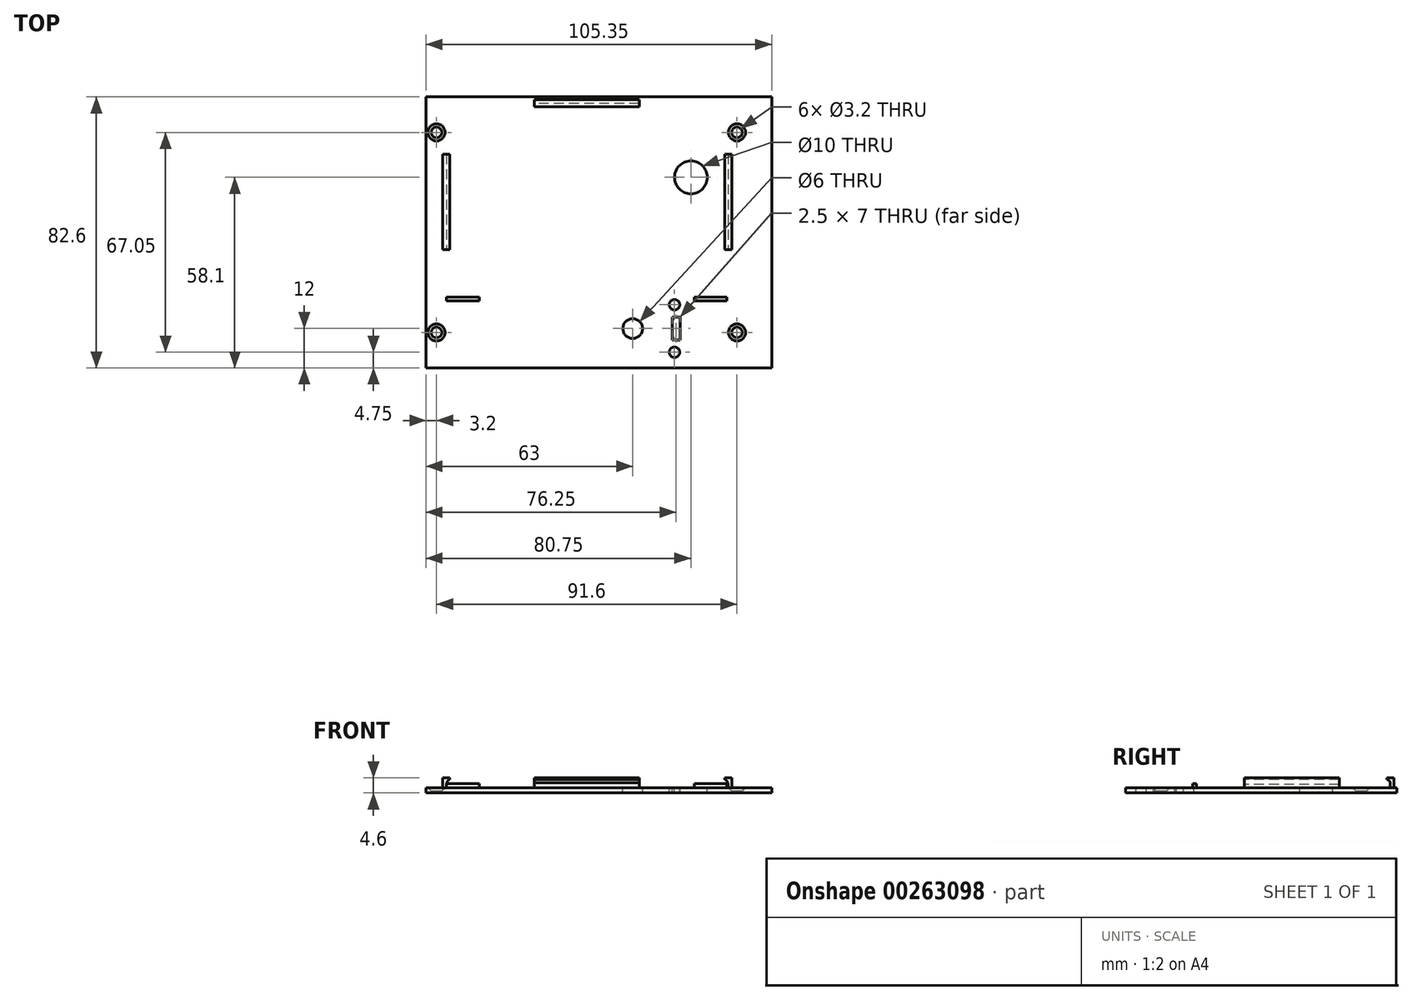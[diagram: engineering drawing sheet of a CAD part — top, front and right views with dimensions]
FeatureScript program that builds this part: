
annotation { "Feature Type Name" : "Feature", "Feature Type Description" : "" }
export const myFeature = defineFeature(function(context is Context, id is Id, definition is map)
    precondition{}
    {
        {
            var Q0;
            Q0=qCreatedBy(makeId("Top.planeOp"),FACE);
            var sketch = newSketch(context, id + "F0", { "sketchPlane" : qUnion([Q0])});
            skLineSegment(sketch, "E0.bottom", {"start": v(0, 0) * mm, "end": v(105.35, 0) * mm});
            skLineSegment(sketch, "E0.top", {"start": v(0, 82.6) * mm, "end": v(105.35, 82.6) * mm});
            skLineSegment(sketch, "E0.left", {"start": v(0, 0) * mm, "end": v(0, 82.6) * mm});
            skLineSegment(sketch, "E0.right", {"start": v(105.35, 0) * mm, "end": v(105.35, 82.6) * mm});
            skLineSegment(sketch, "E1.bottom", {"start": v(3.2, 71.8) * mm, "end": v(94.8, 71.8) * mm, "construction": true});
            skLineSegment(sketch, "E1.top", {"start": v(3.2, 10.8) * mm, "end": v(94.8, 10.8) * mm, "construction": true});
            skLineSegment(sketch, "E1.left", {"start": v(3.2, 71.8) * mm, "end": v(3.2, 10.8) * mm, "construction": true});
            skLineSegment(sketch, "E1.right", {"start": v(94.8, 71.8) * mm, "end": v(94.8, 10.8) * mm, "construction": true});
            skCircle(sketch, "E2", {"center": v(3.2, 71.8) * mm, "radius": 1.6 * mm});
            skCircle(sketch, "E3", {"center": v(94.8, 71.8) * mm, "radius": 1.6 * mm});
            skCircle(sketch, "E4", {"center": v(94.8, 10.8) * mm, "radius": 1.6 * mm});
            skCircle(sketch, "E5", {"center": v(3.2, 10.8) * mm, "radius": 1.6 * mm});
            skSolve(sketch);
        }
        {
            var Q0;
            Q0=makeQuery(id+"F0.imprint","IMPRINT",FACE,{"disambiguationData":[TD([[makeQuery(id+"F0.imprint","IMPRINT",EDGE,{"derivedFrom":sQuery(id+"F0.wireOp",EDGE,"E0.bottom")}),1.0]])]});
            var sketch = newSketch(context, id + "F1", { "sketchPlane" : qUnion([Q0])});
            skLineSegment(sketch, "E6.bottom", {"start": v(6.25, 80.6) * mm, "end": v(91.75, 80.6) * mm, "construction": true});
            skLineSegment(sketch, "E6.top", {"start": v(6.25, 21.6) * mm, "end": v(91.75, 21.6) * mm, "construction": true});
            skLineSegment(sketch, "E6.left", {"start": v(6.25, 80.6) * mm, "end": v(6.25, 21.6) * mm, "construction": true});
            skLineSegment(sketch, "E6.right", {"start": v(91.75, 80.6) * mm, "end": v(91.75, 21.6) * mm, "construction": true});
            skCircle(sketch, "E7", {"center": v(80.75, 58.1) * mm, "radius": 5 * mm});
            skLineSegment(sketch, "E8", {"start": v(49, 80.6) * mm, "end": v(49, 21.6) * mm, "construction": true});
            skLineSegment(sketch, "E9.bottom", {"start": v(6.25, 21.6) * mm, "end": v(16.25, 21.6) * mm});
            skLineSegment(sketch, "E9.top", {"start": v(6.25, 20.4) * mm, "end": v(16.25, 20.4) * mm});
            skLineSegment(sketch, "E9.left", {"start": v(6.25, 21.6) * mm, "end": v(6.25, 20.4) * mm});
            skLineSegment(sketch, "E9.right", {"start": v(16.25, 21.6) * mm, "end": v(16.25, 20.4) * mm});
            skLineSegment(sketch, "E10.bottom", {"start": v(91.75, 21.6) * mm, "end": v(81.75, 21.6) * mm});
            skLineSegment(sketch, "E10.top", {"start": v(91.75, 20.4) * mm, "end": v(81.75, 20.4) * mm});
            skLineSegment(sketch, "E10.left", {"start": v(91.75, 21.6) * mm, "end": v(91.75, 20.4) * mm});
            skLineSegment(sketch, "E10.right", {"start": v(81.75, 21.6) * mm, "end": v(81.75, 20.4) * mm});
            skSolve(sketch);
        }
        {
            var Q0;
            Q0=makeQuery(id+"F0.imprint","IMPRINT",FACE,{"disambiguationData":[TD([[makeQuery(id+"F0.imprint","IMPRINT",EDGE,{"derivedFrom":sQuery(id+"F0.wireOp",EDGE,"E0.bottom")}),1.0]])]});
            var sketch = newSketch(context, id + "F2", { "sketchPlane" : qUnion([Q0])});
            skLineSegment(sketch, "E11.bottom", {"start": v(53.5, 22.5) * mm, "end": v(82.5, 22.5) * mm, "construction": true});
            skLineSegment(sketch, "E11.top", {"start": v(53.5, 1.5) * mm, "end": v(82.5, 1.5) * mm, "construction": true});
            skLineSegment(sketch, "E11.left", {"start": v(53.5, 22.5) * mm, "end": v(53.5, 1.5) * mm, "construction": true});
            skLineSegment(sketch, "E11.right", {"start": v(82.5, 22.5) * mm, "end": v(82.5, 1.5) * mm, "construction": true});
            skCircle(sketch, "E12", {"center": v(75.75, 19.25) * mm, "radius": 1.6 * mm});
            skCircle(sketch, "E13", {"center": v(75.75, 4.75) * mm, "radius": 1.6 * mm});
            skCircle(sketch, "E14", {"center": v(63, 12) * mm, "radius": 3 * mm});
            skLineSegment(sketch, "E15.bottom", {"start": v(75, 15.5) * mm, "end": v(77.5, 15.5) * mm});
            skLineSegment(sketch, "E15.top", {"start": v(75, 8.5) * mm, "end": v(77.5, 8.5) * mm});
            skLineSegment(sketch, "E15.left", {"start": v(75, 15.5) * mm, "end": v(75, 8.5) * mm});
            skLineSegment(sketch, "E15.right", {"start": v(77.5, 15.5) * mm, "end": v(77.5, 8.5) * mm});
            skSolve(sketch);
        }
        {
            var Q0;
            Q0=makeQuery(id+"F0.imprint","IMPRINT",FACE,{"disambiguationData":[TD([[makeQuery(id+"F0.imprint","IMPRINT",EDGE,{"derivedFrom":sQuery(id+"F0.wireOp",EDGE,"E0.bottom")}),1.0]])]});
            extrude(context, id + "F3", {"entities" : qUnion([Q0]), "oppositeDirection" : true, "depth" : 1.6 * mm});
        }
        {
            var Q0;
            Q0=makeQuery(id+"F1.imprint","IMPRINT",FACE,{"disambiguationData":[TD([[makeQuery(id+"F1.imprint","IMPRINT",EDGE,{"derivedFrom":sQuery(id+"F1.wireOp",EDGE,"E7")}),1.0]])]});
            extrude(context, id + "F4", {"entities" : qUnion([Q0]), "operationType" : NewBodyOperationType.REMOVE, "endBound" : BoundingType.THROUGH_ALL, "oppositeDirection" : true, "depth" : 25 * mm});
        }
        {
            var Q0;
            Q0=makeQuery(id+"F2.imprint","IMPRINT",FACE,{"disambiguationData":[TD([[makeQuery(id+"F2.imprint","IMPRINT",EDGE,{"derivedFrom":sQuery(id+"F2.wireOp",EDGE,"E13")}),1.0]])]});
            var Q1;
            Q1=makeQuery(id+"F2.imprint","IMPRINT",FACE,{"disambiguationData":[TD([[makeQuery(id+"F2.imprint","IMPRINT",EDGE,{"derivedFrom":sQuery(id+"F2.wireOp",EDGE,"E14")}),1.0]])]});
            var Q2;
            Q2=makeQuery(id+"F2.imprint","IMPRINT",FACE,{"disambiguationData":[TD([[makeQuery(id+"F2.imprint","IMPRINT",EDGE,{"derivedFrom":sQuery(id+"F2.wireOp",EDGE,"E15.bottom")}),-1.0]])]});
            var Q3;
            Q3=makeQuery(id+"F2.imprint","IMPRINT",FACE,{"disambiguationData":[TD([[makeQuery(id+"F2.imprint","IMPRINT",EDGE,{"derivedFrom":sQuery(id+"F2.wireOp",EDGE,"E12")}),1.0]])]});
            extrude(context, id + "F5", {"entities" : qUnion([Q0, Q1, Q2, Q3]), "operationType" : NewBodyOperationType.REMOVE, "endBound" : BoundingType.THROUGH_ALL, "oppositeDirection" : true, "depth" : 25 * mm});
        }
        {
            var Q0;
            Q0=qCreatedBy(makeId("Front.planeOp"),FACE);
            var sketch = newSketch(context, id + "F6", { "sketchPlane" : qUnion([Q0])});
            skLineSegment(sketch, "E16", {"start": v(6.25, 0) * mm, "end": v(5.05, 0) * mm});
            skLineSegment(sketch, "E17.bottom", {"start": v(5.05, 0) * mm, "end": v(6.25, 0) * mm});
            skLineSegment(sketch, "E17.top", {"start": v(5.05, 0) * mm, "end": v(6.25, 0) * mm});
            skLineSegment(sketch, "E17.left", {"start": v(5.05, 0) * mm, "end": v(5.05, 0) * mm});
            skLineSegment(sketch, "E17.right", {"start": v(6.25, 0) * mm, "end": v(6.25, 0) * mm});
            skLineSegment(sketch, "E18.bottom", {"start": v(6.25, 3) * mm, "end": v(5.05, 3) * mm});
            skLineSegment(sketch, "E18.left", {"start": v(6.25, 3) * mm, "end": v(6.25, 0) * mm});
            skLineSegment(sketch, "E18.right", {"start": v(5.05, 3) * mm, "end": v(5.05, 0) * mm});
            skLineSegment(sketch, "E19", {"start": v(6.25, 3) * mm, "end": v(7.25, 3) * mm});
            skLineSegment(sketch, "E20", {"start": v(7.25, 3) * mm, "end": v(7.25, 2.5) * mm});
            skFitSpline(sketch, "E21", {"points": [v(7.25, 2.5) * mm, v(6.25, 0) * mm], "startDerivative": vector(-3.78, -0.96) * mm, "endDerivative": vector(0, -0.48) * mm});
            skLineSegment(sketch, "E22", {"start": v(49.15, 0) * mm, "end": v(49.15, 10.87) * mm, "construction": true});
            skLineSegment(sketch, "E23.MirrorCS", {"start": v(92.05, 3) * mm, "end": v(93.25, 3) * mm});
            skLineSegment(sketch, "E24.MirrorCS", {"start": v(92.05, 3) * mm, "end": v(91.05, 3) * mm});
            skLineSegment(sketch, "E25.MirrorCS", {"start": v(91.05, 3) * mm, "end": v(91.05, 2.5) * mm});
            skLineSegment(sketch, "E26.MirrorCS", {"start": v(92.05, 3) * mm, "end": v(92.05, 0) * mm});
            skFitSpline(sketch, "E27.MirrorCS", {"points": [v(91.05, 2.5) * mm, v(92.05, 0) * mm], "startDerivative": vector(3.78, -0.96) * mm, "endDerivative": vector(0, -0.48) * mm});
            skLineSegment(sketch, "E28.MirrorCS", {"start": v(92.05, 0) * mm, "end": v(93.25, 0) * mm});
            skLineSegment(sketch, "E29.MirrorCS", {"start": v(93.25, 3) * mm, "end": v(93.25, 0) * mm});
            skSolve(sketch);
        }
        {
            var Q0;
            Q0=qSketchRegion(id+"F6",true);
            extrude(context, id + "F7", {"entities" : qUnion([Q0]), "operationType" : NewBodyOperationType.ADD, "oppositeDirection" : true, "depth" : 65.1 * mm, "hasSecondDirection" : true, "secondDirectionOppositeDirection" : true, "secondDirectionDepth" : 36.1 * mm});
        }
        {
            var Q0;
            Q0=qCreatedBy(makeId("Right.planeOp"),FACE);
            var sketch = newSketch(context, id + "F8", { "sketchPlane" : qUnion([Q0])});
            skLineSegment(sketch, "E30.bottom", {"start": v(80.62, 0) * mm, "end": v(81.82, 0) * mm});
            skLineSegment(sketch, "E30.top", {"start": v(80.62, 3) * mm, "end": v(81.82, 3) * mm});
            skLineSegment(sketch, "E30.left", {"start": v(80.62, 0) * mm, "end": v(80.62, 3) * mm});
            skLineSegment(sketch, "E30.right", {"start": v(81.82, 0) * mm, "end": v(81.82, 3) * mm});
            skLineSegment(sketch, "E31", {"start": v(80.62, 3) * mm, "end": v(79.62, 3) * mm});
            skLineSegment(sketch, "E32", {"start": v(79.62, 3) * mm, "end": v(79.62, 2.5) * mm});
            skFitSpline(sketch, "E33", {"points": [v(79.62, 2.5) * mm, v(80.62, 1.5) * mm, v(80.62, 0) * mm], "startDerivative": vector(3.74, -1.12) * mm, "endDerivative": vector(0, -1.77) * mm});
            skSolve(sketch);
        }
        {
            var Q0;
            Q0=qSketchRegion(id+"F8",true);
            extrude(context, id + "F9", {"entities" : qUnion([Q0]), "operationType" : NewBodyOperationType.ADD, "depth" : 65 * mm, "hasSecondDirection" : true, "secondDirectionOppositeDirection" : false, "secondDirectionDepth" : 33 * mm});
        }
        {
            var Q0;
            Q0=makeQuery(id+"F1.imprint","IMPRINT",FACE,{"disambiguationData":[TD([[makeQuery(id+"F1.imprint","IMPRINT",EDGE,{"derivedFrom":sQuery(id+"F1.wireOp",EDGE,"E9.bottom")}),-1.0]])]});
            var Q1;
            Q1=makeQuery(id+"F1.imprint","IMPRINT",FACE,{"disambiguationData":[TD([[makeQuery(id+"F1.imprint","IMPRINT",EDGE,{"derivedFrom":sQuery(id+"F1.wireOp",EDGE,"E10.bottom")}),1.0]])]});
            extrude(context, id + "F10", {"entities" : qUnion([Q0, Q1]), "operationType" : NewBodyOperationType.ADD, "depth" : 1.2 * mm});
        }
        {
            var Q0;
            Q0=makeQuery(id+"F3.opExtrude","CAP_EDGE",EDGE,{"disambiguationData":[OSD([sQuery(id+"F0.wireOp",EDGE,"E2")])],"isStart":true});
            var Q1;
            Q1=makeQuery(id+"F3.opExtrude","CAP_EDGE",EDGE,{"disambiguationData":[OSD([sQuery(id+"F0.wireOp",EDGE,"E3")])],"isStart":true});
            var Q2;
            Q2=makeQuery(id+"F3.opExtrude","CAP_EDGE",EDGE,{"disambiguationData":[OSD([sQuery(id+"F0.wireOp",EDGE,"E4")])],"isStart":true});
            var Q3;
            Q3=makeQuery(id+"F5.boolean.opBoolean","COPY",EDGE,{"derivedFrom":makeQuery(id+"F5.opExtrude","CAP_EDGE",EDGE,{"disambiguationData":[OSD([sQuery(id+"F2.wireOp",EDGE,"E12")])],"isStart":true})});
            var Q4;
            Q4=makeQuery(id+"F5.boolean.opBoolean","COPY",EDGE,{"derivedFrom":makeQuery(id+"F5.opExtrude","CAP_EDGE",EDGE,{"disambiguationData":[OSD([sQuery(id+"F2.wireOp",EDGE,"E13")])],"isStart":true})});
            var Q5;
            Q5=makeQuery(id+"F3.opExtrude","CAP_EDGE",EDGE,{"disambiguationData":[OSD([sQuery(id+"F0.wireOp",EDGE,"E5")])],"isStart":true});
            chamfer(context, id + "F11", {"entities" : qUnion([Q0, Q1, Q2, Q3, Q4, Q5]), "width" : 1 * mm, "tangentPropagation" : true});
        }
    });
